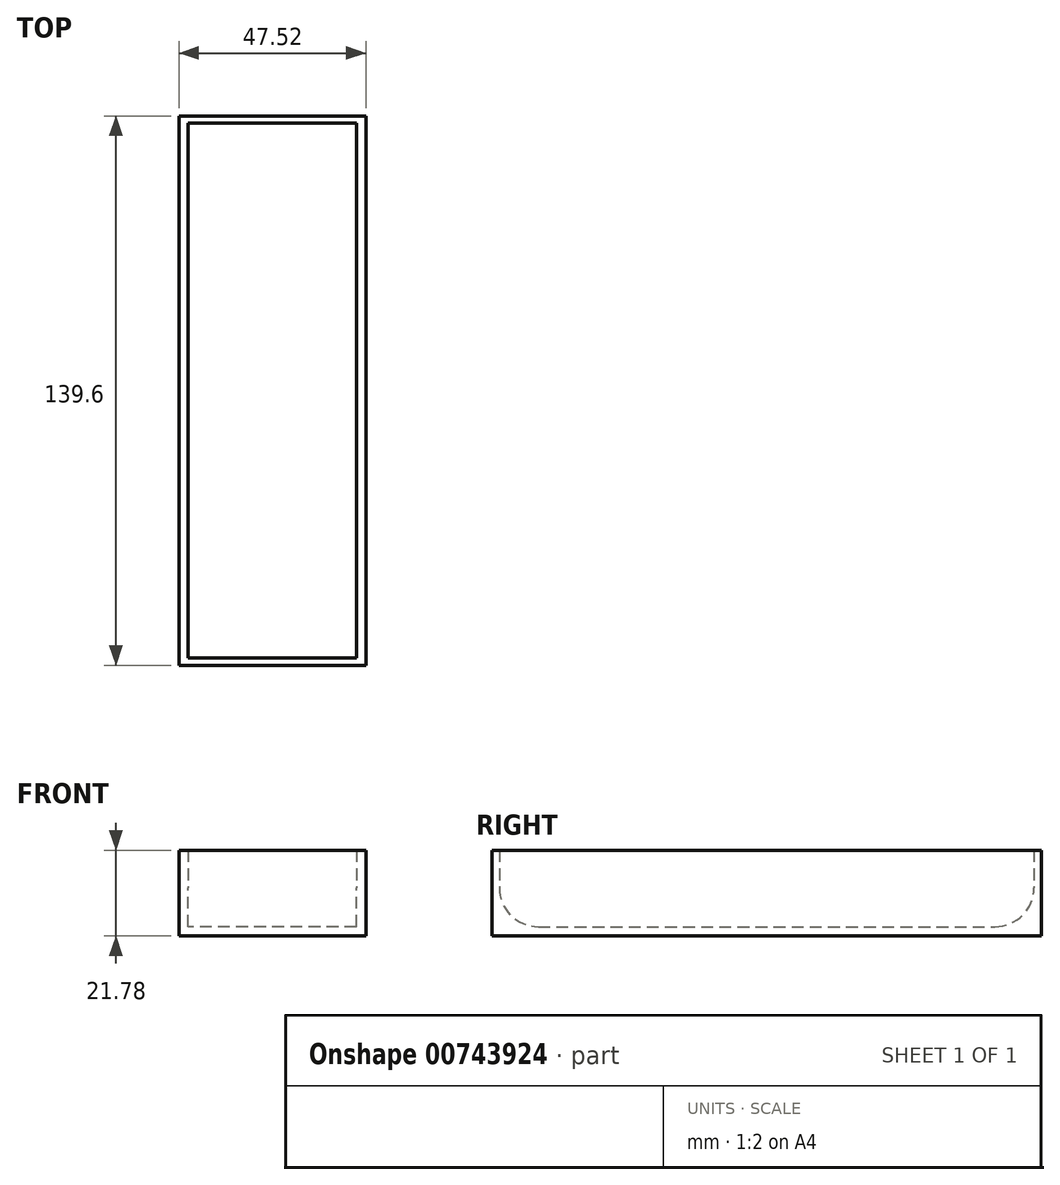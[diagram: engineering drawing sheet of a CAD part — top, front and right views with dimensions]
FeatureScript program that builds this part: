
annotation { "Feature Type Name" : "Feature", "Feature Type Description" : "" }
export const myFeature = defineFeature(function(context is Context, id is Id, definition is map)
    precondition{}
    {
        {
            var Q0;
            Q0=qCreatedBy(makeId("Top.planeOp"),FACE);
            var sketch = newSketch(context, id + "F0", { "sketchPlane" : qUnion([Q0])});
            skLineSegment(sketch, "E0.bottom", {"start": v(24, -70.5) * mm, "end": v(-24, -70.5) * mm});
            skLineSegment(sketch, "E0.top", {"start": v(24, 70.5) * mm, "end": v(-24, 70.5) * mm});
            skLineSegment(sketch, "E0.left", {"start": v(24, -70.5) * mm, "end": v(24, 70.5) * mm});
            skLineSegment(sketch, "E0.right", {"start": v(-24, -70.5) * mm, "end": v(-24, 70.5) * mm});
            skPoint(sketch, "E0.middle", {"position": v(0, 0) * mm});
            skLineSegment(sketch, "E1.bottom", {"start": v(-21.6, 68.6) * mm, "end": v(21.6, 68.6) * mm});
            skLineSegment(sketch, "E1.top", {"start": v(-21.6, -68.6) * mm, "end": v(21.6, -68.6) * mm});
            skLineSegment(sketch, "E1.left", {"start": v(-21.6, 68.6) * mm, "end": v(-21.6, -68.6) * mm});
            skLineSegment(sketch, "E1.right", {"start": v(21.6, 68.6) * mm, "end": v(21.6, -68.6) * mm});
            skSolve(sketch);
        }
        {
            var Q0;
            Q0=makeQuery(id+"F0.imprint","IMPRINT",FACE,{"disambiguationData":[TD([[makeQuery(id+"F0.imprint","IMPRINT",EDGE,{"derivedFrom":sQuery(id+"F0.wireOp",EDGE,"E1.bottom")}),-1.0]])]});
            var Q1;
            Q1=makeQuery(id+"F0.imprint","IMPRINT",FACE,{"disambiguationData":[TD([[makeQuery(id+"F0.imprint","IMPRINT",EDGE,{"derivedFrom":sQuery(id+"F0.wireOp",EDGE,"E0.bottom")}),-1.0]])]});
            extrude(context, id + "F1", {"entities" : qUnion([Q0, Q1]), "depth" : 2.4 * mm, "offsetDistance" : 25 * mm});
        }
        {
            var Q0;
            Q0=makeQuery(id+"F0.imprint","IMPRINT",FACE,{"disambiguationData":[TD([[makeQuery(id+"F0.imprint","IMPRINT",EDGE,{"derivedFrom":sQuery(id+"F0.wireOp",EDGE,"E0.bottom")}),-1.0]])]});
            extrude(context, id + "F2", {"entities" : qUnion([Q0]), "operationType" : NewBodyOperationType.ADD, "depth" : 22 * mm, "offsetDistance" : 25 * mm});
        }
        {
            var Q0;
            Q0=makeQuery(id+"F2.boolean.opBoolean","INTERSECT",EDGE,{"derivedFrom":[makeQuery(id+"F1.opExtrude","CAP_FACE",FACE,{"disambiguationData":[OSD([sQuery(id+"F0.wireOp",EDGE,"E0.bottom"),sQuery(id+"F0.wireOp",EDGE,"E0.top"),sQuery(id+"F0.wireOp",EDGE,"E0.left"),sQuery(id+"F0.wireOp",EDGE,"E0.right")])],"isStart":false}),makeQuery(id+"F2.opExtrude","SWEPT_FACE",FACE,{"disambiguationData":[OSD([sQuery(id+"F0.wireOp",EDGE,"E1.top")])]})]});
            var Q1;
            Q1=makeQuery(id+"F2.boolean.opBoolean","INTERSECT",EDGE,{"derivedFrom":[makeQuery(id+"F1.opExtrude","CAP_FACE",FACE,{"disambiguationData":[OSD([sQuery(id+"F0.wireOp",EDGE,"E0.bottom"),sQuery(id+"F0.wireOp",EDGE,"E0.top"),sQuery(id+"F0.wireOp",EDGE,"E0.left"),sQuery(id+"F0.wireOp",EDGE,"E0.right")])],"isStart":false}),makeQuery(id+"F2.opExtrude","SWEPT_FACE",FACE,{"disambiguationData":[OSD([sQuery(id+"F0.wireOp",EDGE,"E1.bottom")])]})]});
            fillet(context, id + "F3", {"entities" : qUnion([Q0, Q1]), "radius" : 10 * mm, "tangentPropagation" : true, "allowEdgeOverflow" : false});
        }
        {
            var Q0;
            Q0=makeQuery(id+"F1.opExtrude","SWEPT_BODY",BODY,{"disambiguationData":[OSD([sQuery(id+"F0.wireOp",EDGE,"E0.bottom"),sQuery(id+"F0.wireOp",EDGE,"E0.top"),sQuery(id+"F0.wireOp",EDGE,"E0.left"),sQuery(id+"F0.wireOp",EDGE,"E0.right")])]});
            var Q1;
            Q1=sQuery(id+"F0.wireOp",VERTEX,"E0.middle");
            transform(context, id + "F4", {"entities" : qUnion([Q0]), "transformType" : TransformType.SCALE_UNIFORMLY, "scale" : .99, "scalePoint" : qUnion([Q1]), "makeCopy" : false});
        }
    });
